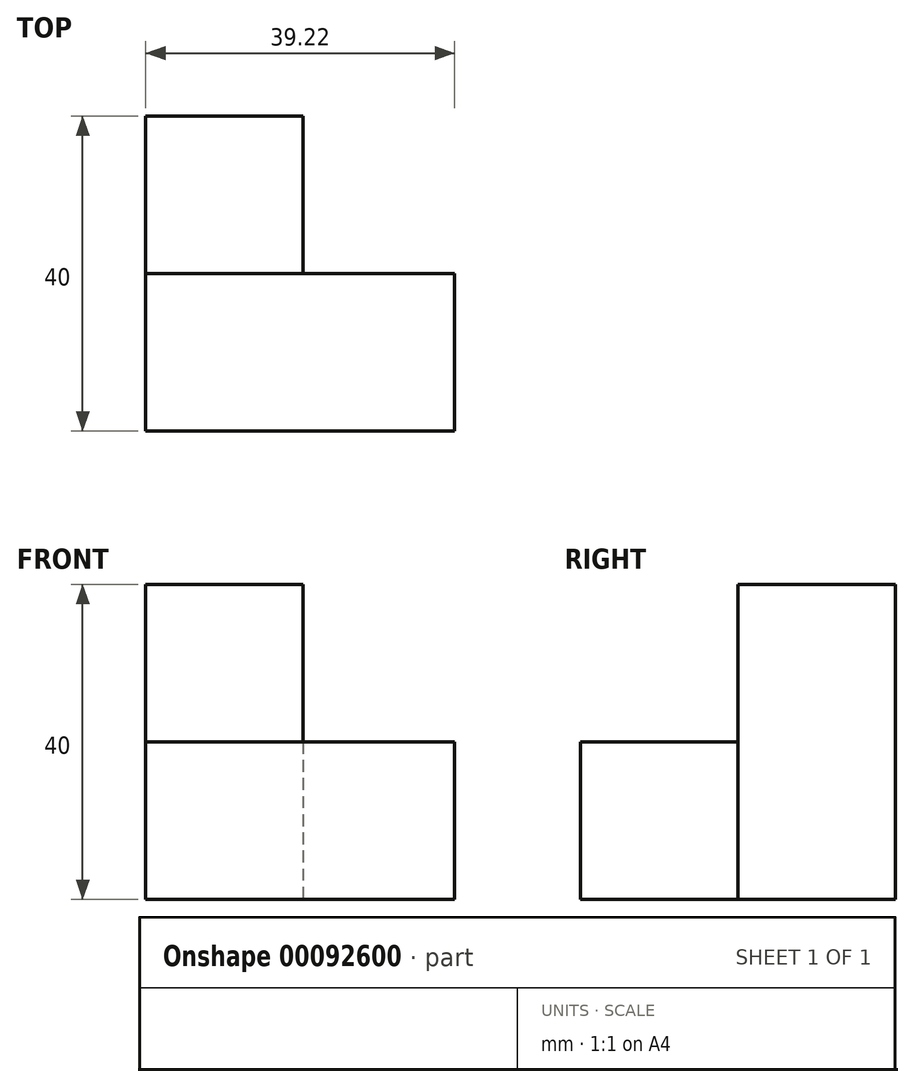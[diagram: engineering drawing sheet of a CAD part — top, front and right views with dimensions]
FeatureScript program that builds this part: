
annotation { "Feature Type Name" : "Feature", "Feature Type Description" : "" }
export const myFeature = defineFeature(function(context is Context, id is Id, definition is map)
    precondition{}
    {
        {
            var Q0;
            Q0=qCreatedBy(makeId("Top.planeOp"),FACE);
            var sketch = newSketch(context, id + "F0", { "sketchPlane" : qUnion([Q0])});
            skLineSegment(sketch, "E0.bottom", {"start": v(-20, 0) * mm, "end": v(0, 0) * mm});
            skLineSegment(sketch, "E0.top", {"start": v(-20, -40) * mm, "end": v(0, -40) * mm});
            skLineSegment(sketch, "E0.left", {"start": v(-20, 0) * mm, "end": v(-20, -40) * mm});
            skLineSegment(sketch, "E0.right", {"start": v(0, 0) * mm, "end": v(0, -20) * mm});
            skLineSegment(sketch, "E1.bottom", {"start": v(0, -20) * mm, "end": v(19.22, -20) * mm});
            skLineSegment(sketch, "E1.top", {"start": v(-0.78, -40) * mm, "end": v(19.22, -40) * mm});
            skLineSegment(sketch, "E1.right", {"start": v(19.22, -20) * mm, "end": v(19.22, -40) * mm});
            skSolve(sketch);
        }
        {
            var Q0;
            Q0=makeQuery(id+"F0.imprint","IMPRINT",FACE,{"disambiguationData":[TD([[makeQuery(id+"F0.imprint","IMPRINT",EDGE,{"derivedFrom":sQuery(id+"F0.wireOp",EDGE,"E0.bottom")}),-1.0]])]});
            extrude(context, id + "F1", {"entities" : qUnion([Q0]), "depth" : 20 * mm});
        }
        {
            var Q0;
            Q0=makeQuery(id+"F1.opExtrude","CAP_FACE",FACE,{"disambiguationData":[OSD([sQuery(id+"F0.wireOp",EDGE,"E0.bottom"),sQuery(id+"F0.wireOp",EDGE,"E0.top"),sQuery(id+"F0.wireOp",EDGE,"E0.left"),sQuery(id+"F0.wireOp",EDGE,"E0.right"),sQuery(id+"F0.wireOp",EDGE,"E1.bottom"),sQuery(id+"F0.wireOp",EDGE,"E1.top"),sQuery(id+"F0.wireOp",EDGE,"E1.right")])],"isStart":false});
            var sketch = newSketch(context, id + "F2", { "sketchPlane" : qUnion([Q0])});
            skLineSegment(sketch, "E2.bottom", {"start": v(-20, 0) * mm, "end": v(0, 0) * mm});
            skLineSegment(sketch, "E2.top", {"start": v(-20, -20) * mm, "end": v(0, -20) * mm});
            skLineSegment(sketch, "E2.left", {"start": v(-20, 0) * mm, "end": v(-20, -20) * mm});
            skLineSegment(sketch, "E2.right", {"start": v(0, 0) * mm, "end": v(0, -20) * mm});
            skSolve(sketch);
        }
        {
            var Q0;
            Q0=makeQuery(id+"F2.imprint","IMPRINT",FACE,{"disambiguationData":[TD([[makeQuery(id+"F2.imprint","IMPRINT",EDGE,{"derivedFrom":sQuery(id+"F2.wireOp",EDGE,"E2.bottom")}),-1.0]])]});
            extrude(context, id + "F3", {"entities" : qUnion([Q0]), "operationType" : NewBodyOperationType.ADD, "depth" : 20 * mm});
        }
    });
